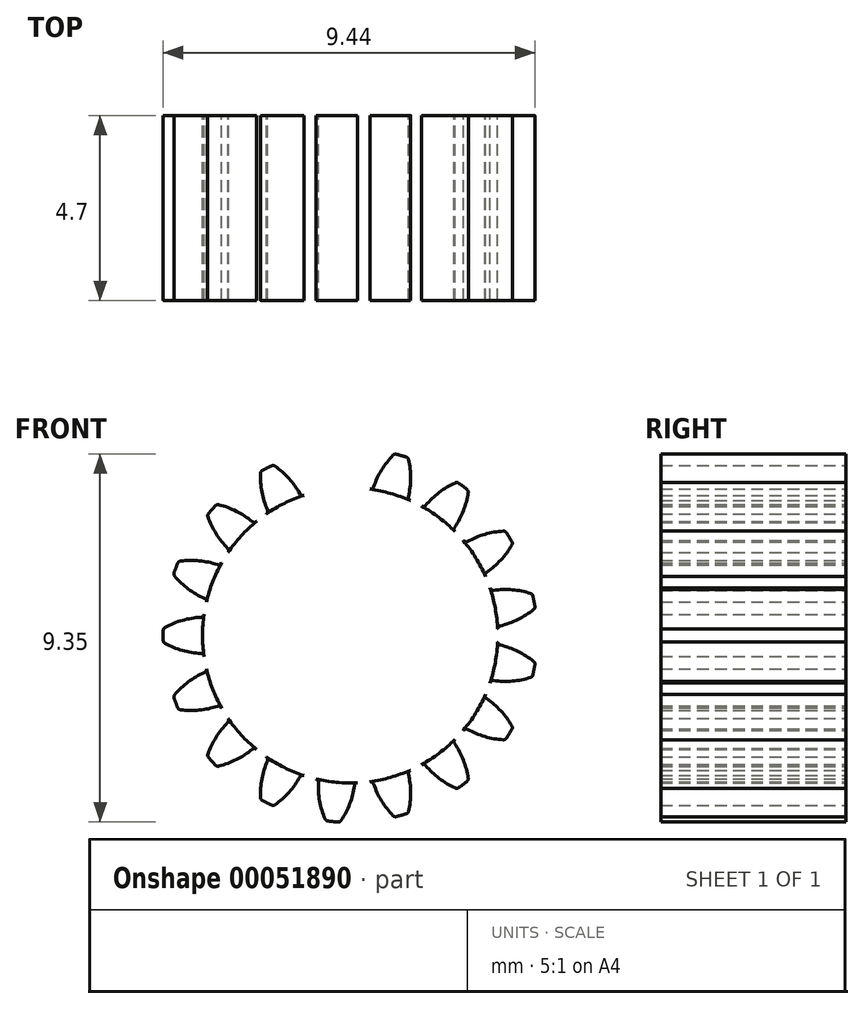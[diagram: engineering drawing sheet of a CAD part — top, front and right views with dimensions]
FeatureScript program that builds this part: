
annotation { "Feature Type Name" : "Feature", "Feature Type Description" : "" }
export const myFeature = defineFeature(function(context is Context, id is Id, definition is map)
    precondition{}
    {
        {
            var Q0;
            Q0=qCreatedBy(makeId("Front.planeOp"),FACE);
            var sketch = newSketch(context, id + "F0", { "sketchPlane" : qUnion([Q0])});
            skCircle(sketch, "E0", {"center": v(0, 0) * mm, "radius": 3.75 * mm, "construction": true});
            skCircle(sketch, "E1", {"center": v(0, 0) * mm, "radius": 4.25 * mm, "construction": true});
            skCircle(sketch, "E2", {"center": v(0, 0) * mm, "radius": 4.75 * mm, "construction": true});
            skLineSegment(sketch, "E3", {"start": v(0, 0) * mm, "end": v(0, 10.28) * mm, "construction": true});
            skLineSegment(sketch, "E4", {"start": v(0, 0) * mm, "end": v(-1.03, 11.12) * mm, "construction": true});
            skLineSegment(sketch, "E5", {"start": v(0, 4.25) * mm, "end": v(-15.76, 4.25) * mm, "construction": true});
            skLineSegment(sketch, "E6", {"start": v(0, 4.25) * mm, "end": v(-14.39, -0.99) * mm, "construction": true});
            skCircle(sketch, "E7", {"center": v(0, 4.25) * mm, "radius": 2.12 * mm, "construction": true});
            skCircle(sketch, "E8", {"center": v(-2, 3.52) * mm, "radius": 2.12 * mm, "construction": true});
            skArc(sketch, "E9", {"start": v(-0.23, 4.7) * mm, "mid": v(-0.01, 4.28) * mm, "end": v(0.1, 3.82) * mm});
            skArc(sketch, "E10.MirrorCS", {"start": v(-0.64, 4.66) * mm, "mid": v(-0.78, 4.2) * mm, "end": v(-0.8, 3.73) * mm});
            skArc(sketch, "E11", {"start": v(-0.57, 4.72) * mm, "mid": v(-0.44, 4.73) * mm, "end": v(-0.3, 4.74) * mm});
            skArc(sketch, "E12", {"start": v(-0.87, 3.65) * mm, "mid": v(0.35, -3.73) * mm, "end": v(0.19, 3.75) * mm});
            skPoint(sketch, "E13.visualSharp", {"position": v(-0.8, 3.66) * mm});
            skArc(sketch, "E13.filletArc", {"start": v(-0.87, 3.65) * mm, "mid": v(-0.82, 3.68) * mm, "end": v(-0.8, 3.73) * mm});
            skPoint(sketch, "E14.visualSharp", {"position": v(-0.62, 4.7) * mm});
            skArc(sketch, "E14.filletArc", {"start": v(-0.57, 4.72) * mm, "mid": v(-0.61, 4.7) * mm, "end": v(-0.64, 4.66) * mm});
            skPoint(sketch, "E15.visualSharp", {"position": v(-0.26, 4.74) * mm});
            skArc(sketch, "E15.filletArc", {"start": v(-0.23, 4.7) * mm, "mid": v(-0.26, 4.73) * mm, "end": v(-0.3, 4.74) * mm});
            skPoint(sketch, "E16.visualSharp", {"position": v(0.12, 3.75) * mm});
            skArc(sketch, "E16.filletArc", {"start": v(0.1, 3.82) * mm, "mid": v(0.13, 3.77) * mm, "end": v(0.19, 3.75) * mm});
            skArc(sketch, "E17.1.0", {"start": v(-2.13, 3.09) * mm, "mid": v(-2.1, 3.13) * mm, "end": v(-2.1, 3.19) * mm});
            skArc(sketch, "E17.1.1", {"start": v(-2.28, 4.12) * mm, "mid": v(-2.24, 3.64) * mm, "end": v(-2.1, 3.19) * mm});
            skArc(sketch, "E17.1.2", {"start": v(-2.24, 4.2) * mm, "mid": v(-2.27, 4.16) * mm, "end": v(-2.28, 4.12) * mm});
            skArc(sketch, "E17.1.3", {"start": v(-2.24, 4.2) * mm, "mid": v(-2.12, 4.25) * mm, "end": v(-2, 4.3) * mm});
            skArc(sketch, "E17.1.4", {"start": v(-1.91, 4.3) * mm, "mid": v(-1.95, 4.32) * mm, "end": v(-2, 4.3) * mm});
            skArc(sketch, "E17.1.5", {"start": v(-1.91, 4.3) * mm, "mid": v(-1.56, 3.99) * mm, "end": v(-1.28, 3.6) * mm});
            skArc(sketch, "E17.1.6", {"start": v(-1.28, 3.6) * mm, "mid": v(-1.24, 3.56) * mm, "end": v(-1.18, 3.56) * mm});
            skArc(sketch, "E17.2.0", {"start": v(-3.1, 2.1) * mm, "mid": v(-3.09, 2.16) * mm, "end": v(-3.11, 2.22) * mm});
            skArc(sketch, "E17.2.1", {"start": v(-3.61, 3.02) * mm, "mid": v(-3.4, 2.59) * mm, "end": v(-3.11, 2.22) * mm});
            skArc(sketch, "E17.2.2", {"start": v(-3.6, 3.1) * mm, "mid": v(-3.62, 3.06) * mm, "end": v(-3.61, 3.02) * mm});
            skArc(sketch, "E17.2.3", {"start": v(-3.6, 3.1) * mm, "mid": v(-3.51, 3.2) * mm, "end": v(-3.42, 3.3) * mm});
            skArc(sketch, "E17.2.4", {"start": v(-3.34, 3.32) * mm, "mid": v(-3.38, 3.32) * mm, "end": v(-3.42, 3.3) * mm});
            skArc(sketch, "E17.2.5", {"start": v(-3.34, 3.32) * mm, "mid": v(-2.9, 3.16) * mm, "end": v(-2.5, 2.9) * mm});
            skArc(sketch, "E17.2.6", {"start": v(-2.5, 2.9) * mm, "mid": v(-2.44, 2.87) * mm, "end": v(-2.38, 2.9) * mm});
            skArc(sketch, "E17.3.0", {"start": v(-3.65, 0.84) * mm, "mid": v(-3.66, 0.9) * mm, "end": v(-3.7, 0.94) * mm});
            skArc(sketch, "E17.3.1", {"start": v(-4.46, 1.5) * mm, "mid": v(-4.11, 1.18) * mm, "end": v(-3.7, 0.94) * mm});
            skArc(sketch, "E17.3.2", {"start": v(-4.48, 1.6) * mm, "mid": v(-4.48, 1.55) * mm, "end": v(-4.46, 1.5) * mm});
            skArc(sketch, "E17.3.3", {"start": v(-4.48, 1.6) * mm, "mid": v(-4.43, 1.72) * mm, "end": v(-4.38, 1.84) * mm});
            skArc(sketch, "E17.3.4", {"start": v(-4.31, 1.9) * mm, "mid": v(-4.35, 1.87) * mm, "end": v(-4.38, 1.84) * mm});
            skArc(sketch, "E17.3.5", {"start": v(-4.31, 1.9) * mm, "mid": v(-3.84, 1.9) * mm, "end": v(-3.37, 1.8) * mm});
            skArc(sketch, "E17.3.6", {"start": v(-3.37, 1.8) * mm, "mid": v(-3.31, 1.8) * mm, "end": v(-3.27, 1.84) * mm});
            skArc(sketch, "E17.4.0", {"start": v(-3.71, -0.53) * mm, "mid": v(-3.74, -0.48) * mm, "end": v(-3.8, -0.46) * mm});
            skArc(sketch, "E17.4.1", {"start": v(-4.7, -0.2) * mm, "mid": v(-4.26, -0.38) * mm, "end": v(-3.8, -0.46) * mm});
            skArc(sketch, "E17.4.2", {"start": v(-4.75, -0.13) * mm, "mid": v(-4.74, -0.18) * mm, "end": v(-4.7, -0.2) * mm});
            skArc(sketch, "E17.4.3", {"start": v(-4.75, -0.13) * mm, "mid": v(-4.75, 0) * mm, "end": v(-4.75, 0.13) * mm});
            skArc(sketch, "E17.4.4", {"start": v(-4.7, 0.2) * mm, "mid": v(-4.74, 0.18) * mm, "end": v(-4.75, 0.13) * mm});
            skArc(sketch, "E17.4.5", {"start": v(-4.7, 0.2) * mm, "mid": v(-4.26, 0.38) * mm, "end": v(-3.8, 0.46) * mm});
            skArc(sketch, "E17.4.6", {"start": v(-3.8, 0.46) * mm, "mid": v(-3.74, 0.48) * mm, "end": v(-3.71, 0.53) * mm});
            skArc(sketch, "E17.5.0", {"start": v(-3.27, -1.84) * mm, "mid": v(-3.31, -1.8) * mm, "end": v(-3.37, -1.8) * mm});
            skArc(sketch, "E17.5.1", {"start": v(-4.31, -1.9) * mm, "mid": v(-3.84, -1.9) * mm, "end": v(-3.37, -1.8) * mm});
            skArc(sketch, "E17.5.2", {"start": v(-4.38, -1.84) * mm, "mid": v(-4.35, -1.87) * mm, "end": v(-4.31, -1.9) * mm});
            skArc(sketch, "E17.5.3", {"start": v(-4.38, -1.84) * mm, "mid": v(-4.43, -1.72) * mm, "end": v(-4.48, -1.6) * mm});
            skArc(sketch, "E17.5.4", {"start": v(-4.46, -1.5) * mm, "mid": v(-4.48, -1.55) * mm, "end": v(-4.48, -1.6) * mm});
            skArc(sketch, "E17.5.5", {"start": v(-4.46, -1.5) * mm, "mid": v(-4.11, -1.18) * mm, "end": v(-3.7, -0.94) * mm});
            skArc(sketch, "E17.5.6", {"start": v(-3.7, -0.94) * mm, "mid": v(-3.66, -0.9) * mm, "end": v(-3.65, -0.84) * mm});
            skArc(sketch, "E17.6.0", {"start": v(-2.38, -2.9) * mm, "mid": v(-2.44, -2.87) * mm, "end": v(-2.5, -2.9) * mm});
            skArc(sketch, "E17.6.1", {"start": v(-3.34, -3.32) * mm, "mid": v(-2.9, -3.16) * mm, "end": v(-2.5, -2.9) * mm});
            skArc(sketch, "E17.6.2", {"start": v(-3.42, -3.3) * mm, "mid": v(-3.38, -3.32) * mm, "end": v(-3.34, -3.32) * mm});
            skArc(sketch, "E17.6.3", {"start": v(-3.42, -3.3) * mm, "mid": v(-3.51, -3.2) * mm, "end": v(-3.6, -3.1) * mm});
            skArc(sketch, "E17.6.4", {"start": v(-3.61, -3.02) * mm, "mid": v(-3.62, -3.06) * mm, "end": v(-3.6, -3.1) * mm});
            skArc(sketch, "E17.6.5", {"start": v(-3.61, -3.02) * mm, "mid": v(-3.4, -2.59) * mm, "end": v(-3.11, -2.22) * mm});
            skArc(sketch, "E17.6.6", {"start": v(-3.11, -2.22) * mm, "mid": v(-3.09, -2.16) * mm, "end": v(-3.1, -2.1) * mm});
            skArc(sketch, "E17.7.0", {"start": v(-1.18, -3.56) * mm, "mid": v(-1.24, -3.56) * mm, "end": v(-1.28, -3.6) * mm});
            skArc(sketch, "E17.7.1", {"start": v(-1.91, -4.3) * mm, "mid": v(-1.56, -3.99) * mm, "end": v(-1.28, -3.6) * mm});
            skArc(sketch, "E17.7.2", {"start": v(-2, -4.3) * mm, "mid": v(-1.95, -4.32) * mm, "end": v(-1.91, -4.3) * mm});
            skArc(sketch, "E17.7.3", {"start": v(-2, -4.3) * mm, "mid": v(-2.12, -4.25) * mm, "end": v(-2.24, -4.2) * mm});
            skArc(sketch, "E17.7.4", {"start": v(-2.28, -4.12) * mm, "mid": v(-2.27, -4.16) * mm, "end": v(-2.24, -4.2) * mm});
            skArc(sketch, "E17.7.5", {"start": v(-2.28, -4.12) * mm, "mid": v(-2.24, -3.64) * mm, "end": v(-2.1, -3.19) * mm});
            skArc(sketch, "E17.7.6", {"start": v(-2.1, -3.19) * mm, "mid": v(-2.1, -3.13) * mm, "end": v(-2.13, -3.09) * mm});
            skArc(sketch, "E17.8.0", {"start": v(0.19, -3.75) * mm, "mid": v(0.13, -3.77) * mm, "end": v(0.1, -3.82) * mm});
            skArc(sketch, "E17.8.1", {"start": v(-0.23, -4.7) * mm, "mid": v(-0.01, -4.28) * mm, "end": v(0.1, -3.82) * mm});
            skArc(sketch, "E17.8.2", {"start": v(-0.3, -4.74) * mm, "mid": v(-0.26, -4.73) * mm, "end": v(-0.23, -4.7) * mm});
            skArc(sketch, "E17.8.3", {"start": v(-0.3, -4.74) * mm, "mid": v(-0.44, -4.73) * mm, "end": v(-0.57, -4.72) * mm});
            skArc(sketch, "E17.8.4", {"start": v(-0.64, -4.66) * mm, "mid": v(-0.61, -4.7) * mm, "end": v(-0.57, -4.72) * mm});
            skArc(sketch, "E17.8.5", {"start": v(-0.64, -4.66) * mm, "mid": v(-0.78, -4.2) * mm, "end": v(-0.8, -3.73) * mm});
            skArc(sketch, "E17.8.6", {"start": v(-0.8, -3.73) * mm, "mid": v(-0.82, -3.68) * mm, "end": v(-0.87, -3.65) * mm});
            skArc(sketch, "E17.9.0", {"start": v(1.53, -3.42) * mm, "mid": v(1.49, -3.46) * mm, "end": v(1.48, -3.52) * mm});
            skArc(sketch, "E17.9.1", {"start": v(1.49, -4.47) * mm, "mid": v(1.54, -4) * mm, "end": v(1.48, -3.52) * mm});
            skArc(sketch, "E17.9.2", {"start": v(1.43, -4.53) * mm, "mid": v(1.46, -4.5) * mm, "end": v(1.49, -4.47) * mm});
            skArc(sketch, "E17.9.3", {"start": v(1.43, -4.53) * mm, "mid": v(1.3, -4.57) * mm, "end": v(1.17, -4.6) * mm});
            skArc(sketch, "E17.9.4", {"start": v(1.09, -4.58) * mm, "mid": v(1.13, -4.6) * mm, "end": v(1.17, -4.6) * mm});
            skArc(sketch, "E17.9.5", {"start": v(1.09, -4.58) * mm, "mid": v(0.8, -4.2) * mm, "end": v(0.6, -3.77) * mm});
            skArc(sketch, "E17.9.6", {"start": v(0.6, -3.77) * mm, "mid": v(0.56, -3.73) * mm, "end": v(0.5, -3.72) * mm});
            skArc(sketch, "E17.10.0", {"start": v(2.66, -2.64) * mm, "mid": v(2.64, -2.7) * mm, "end": v(2.65, -2.75) * mm});
            skArc(sketch, "E17.10.1", {"start": v(3, -3.63) * mm, "mid": v(2.87, -3.17) * mm, "end": v(2.65, -2.75) * mm});
            skArc(sketch, "E17.10.2", {"start": v(2.97, -3.7) * mm, "mid": v(3, -3.67) * mm, "end": v(3, -3.63) * mm});
            skArc(sketch, "E17.10.3", {"start": v(2.97, -3.7) * mm, "mid": v(2.86, -3.8) * mm, "end": v(2.75, -3.87) * mm});
            skArc(sketch, "E17.10.4", {"start": v(2.67, -3.88) * mm, "mid": v(2.71, -3.88) * mm, "end": v(2.75, -3.87) * mm});
            skArc(sketch, "E17.10.5", {"start": v(2.67, -3.88) * mm, "mid": v(2.26, -3.63) * mm, "end": v(1.92, -3.3) * mm});
            skArc(sketch, "E17.10.6", {"start": v(1.92, -3.3) * mm, "mid": v(1.87, -3.27) * mm, "end": v(1.81, -3.28) * mm});
            skArc(sketch, "E17.11.0", {"start": v(3.44, -1.5) * mm, "mid": v(3.43, -1.56) * mm, "end": v(3.47, -1.6) * mm});
            skArc(sketch, "E17.11.1", {"start": v(4.1, -2.3) * mm, "mid": v(3.83, -1.92) * mm, "end": v(3.47, -1.6) * mm});
            skArc(sketch, "E17.11.2", {"start": v(4.1, -2.39) * mm, "mid": v(4.12, -2.34) * mm, "end": v(4.1, -2.3) * mm});
            skArc(sketch, "E17.11.3", {"start": v(4.1, -2.39) * mm, "mid": v(4.04, -2.5) * mm, "end": v(3.97, -2.61) * mm});
            skArc(sketch, "E17.11.4", {"start": v(3.9, -2.65) * mm, "mid": v(3.93, -2.64) * mm, "end": v(3.97, -2.61) * mm});
            skArc(sketch, "E17.11.5", {"start": v(3.9, -2.65) * mm, "mid": v(3.42, -2.57) * mm, "end": v(2.98, -2.39) * mm});
            skArc(sketch, "E17.11.6", {"start": v(2.98, -2.39) * mm, "mid": v(2.93, -2.38) * mm, "end": v(2.88, -2.4) * mm});
            skArc(sketch, "E17.12.0", {"start": v(3.75, -0.16) * mm, "mid": v(3.76, -0.21) * mm, "end": v(3.81, -0.25) * mm});
            skArc(sketch, "E17.12.1", {"start": v(4.66, -0.66) * mm, "mid": v(4.26, -0.4) * mm, "end": v(3.81, -0.25) * mm});
            skArc(sketch, "E17.12.2", {"start": v(4.7, -0.74) * mm, "mid": v(4.69, -0.7) * mm, "end": v(4.66, -0.66) * mm});
            skArc(sketch, "E17.12.3", {"start": v(4.7, -0.74) * mm, "mid": v(4.67, -0.87) * mm, "end": v(4.64, -1) * mm});
            skArc(sketch, "E17.12.4", {"start": v(4.59, -1.07) * mm, "mid": v(4.62, -1.04) * mm, "end": v(4.64, -1) * mm});
            skArc(sketch, "E17.12.5", {"start": v(4.59, -1.07) * mm, "mid": v(4.12, -1.16) * mm, "end": v(3.64, -1.15) * mm});
            skArc(sketch, "E17.12.6", {"start": v(3.64, -1.15) * mm, "mid": v(3.59, -1.16) * mm, "end": v(3.55, -1.2) * mm});
            skArc(sketch, "E17.13.0", {"start": v(3.55, 1.2) * mm, "mid": v(3.59, 1.16) * mm, "end": v(3.64, 1.15) * mm});
            skArc(sketch, "E17.13.1", {"start": v(4.59, 1.07) * mm, "mid": v(4.12, 1.16) * mm, "end": v(3.64, 1.15) * mm});
            skArc(sketch, "E17.13.2", {"start": v(4.64, 1) * mm, "mid": v(4.62, 1.04) * mm, "end": v(4.59, 1.07) * mm});
            skArc(sketch, "E17.13.3", {"start": v(4.64, 1) * mm, "mid": v(4.67, 0.87) * mm, "end": v(4.7, 0.74) * mm});
            skArc(sketch, "E17.13.4", {"start": v(4.66, 0.66) * mm, "mid": v(4.69, 0.7) * mm, "end": v(4.7, 0.74) * mm});
            skArc(sketch, "E17.13.5", {"start": v(4.66, 0.66) * mm, "mid": v(4.26, 0.4) * mm, "end": v(3.81, 0.25) * mm});
            skArc(sketch, "E17.13.6", {"start": v(3.81, 0.25) * mm, "mid": v(3.76, 0.21) * mm, "end": v(3.75, 0.16) * mm});
            skArc(sketch, "E17.14.0", {"start": v(2.88, 2.4) * mm, "mid": v(2.93, 2.38) * mm, "end": v(2.98, 2.39) * mm});
            skArc(sketch, "E17.14.1", {"start": v(3.9, 2.65) * mm, "mid": v(3.42, 2.57) * mm, "end": v(2.98, 2.39) * mm});
            skArc(sketch, "E17.14.2", {"start": v(3.97, 2.61) * mm, "mid": v(3.93, 2.64) * mm, "end": v(3.9, 2.65) * mm});
            skArc(sketch, "E17.14.3", {"start": v(3.97, 2.61) * mm, "mid": v(4.04, 2.5) * mm, "end": v(4.1, 2.39) * mm});
            skArc(sketch, "E17.14.4", {"start": v(4.1, 2.3) * mm, "mid": v(4.12, 2.34) * mm, "end": v(4.1, 2.39) * mm});
            skArc(sketch, "E17.14.5", {"start": v(4.1, 2.3) * mm, "mid": v(3.83, 1.92) * mm, "end": v(3.47, 1.6) * mm});
            skArc(sketch, "E17.14.6", {"start": v(3.47, 1.6) * mm, "mid": v(3.43, 1.56) * mm, "end": v(3.44, 1.5) * mm});
            skArc(sketch, "E17.15.0", {"start": v(1.81, 3.28) * mm, "mid": v(1.87, 3.27) * mm, "end": v(1.92, 3.3) * mm});
            skArc(sketch, "E17.15.1", {"start": v(2.67, 3.88) * mm, "mid": v(2.26, 3.63) * mm, "end": v(1.92, 3.3) * mm});
            skArc(sketch, "E17.15.2", {"start": v(2.75, 3.87) * mm, "mid": v(2.71, 3.88) * mm, "end": v(2.67, 3.88) * mm});
            skArc(sketch, "E17.15.3", {"start": v(2.75, 3.87) * mm, "mid": v(2.86, 3.8) * mm, "end": v(2.97, 3.7) * mm});
            skArc(sketch, "E17.15.4", {"start": v(3, 3.63) * mm, "mid": v(3, 3.67) * mm, "end": v(2.97, 3.7) * mm});
            skArc(sketch, "E17.15.5", {"start": v(3, 3.63) * mm, "mid": v(2.87, 3.17) * mm, "end": v(2.65, 2.75) * mm});
            skArc(sketch, "E17.15.6", {"start": v(2.65, 2.75) * mm, "mid": v(2.64, 2.7) * mm, "end": v(2.66, 2.64) * mm});
            skArc(sketch, "E17.16.0", {"start": v(0.5, 3.72) * mm, "mid": v(0.56, 3.73) * mm, "end": v(0.6, 3.77) * mm});
            skArc(sketch, "E17.16.1", {"start": v(1.09, 4.58) * mm, "mid": v(0.8, 4.2) * mm, "end": v(0.6, 3.77) * mm});
            skArc(sketch, "E17.16.2", {"start": v(1.17, 4.6) * mm, "mid": v(1.13, 4.6) * mm, "end": v(1.09, 4.58) * mm});
            skArc(sketch, "E17.16.3", {"start": v(1.17, 4.6) * mm, "mid": v(1.3, 4.57) * mm, "end": v(1.43, 4.53) * mm});
            skArc(sketch, "E17.16.4", {"start": v(1.49, 4.47) * mm, "mid": v(1.46, 4.5) * mm, "end": v(1.43, 4.53) * mm});
            skArc(sketch, "E17.16.5", {"start": v(1.49, 4.47) * mm, "mid": v(1.54, 4) * mm, "end": v(1.48, 3.52) * mm});
            skArc(sketch, "E17.16.6", {"start": v(1.48, 3.52) * mm, "mid": v(1.49, 3.46) * mm, "end": v(1.53, 3.42) * mm});
            skSolve(sketch);
        }
        {
            var Q0;
            Q0=makeQuery(id+"F0.imprint","IMPRINT",FACE,{"disambiguationData":[TD([[makeQuery(id+"F0.imprint","IMPRINT",EDGE,{"derivedFrom":sQuery(id+"F0.wireOp",EDGE,"E9")}),-1.0]])]});
            var Q1;
            {var subQ0=sQuery(id+"F0.wireOp",EDGE,"E17.1.0");Q1=makeQuery(id+"F0.imprint","IMPRINT",FACE,{"disambiguationData":[TD([[makeQuery(id+"F0.imprint","IMPRINT",EDGE,{"derivedFrom":subQ0}),-1.0]])]});}
            var Q2;
            {var subQ0=sQuery(id+"F0.wireOp",EDGE,"E17.2.0");Q2=makeQuery(id+"F0.imprint","IMPRINT",FACE,{"disambiguationData":[TD([[makeQuery(id+"F0.imprint","IMPRINT",EDGE,{"derivedFrom":subQ0}),-1.0]])]});}
            var Q3;
            {var subQ0=sQuery(id+"F0.wireOp",EDGE,"E17.3.0");Q3=makeQuery(id+"F0.imprint","IMPRINT",FACE,{"disambiguationData":[TD([[makeQuery(id+"F0.imprint","IMPRINT",EDGE,{"derivedFrom":subQ0}),-1.0]])]});}
            var Q4;
            {var subQ0=sQuery(id+"F0.wireOp",EDGE,"E17.4.0");Q4=makeQuery(id+"F0.imprint","IMPRINT",FACE,{"disambiguationData":[TD([[makeQuery(id+"F0.imprint","IMPRINT",EDGE,{"derivedFrom":subQ0}),-1.0]])]});}
            var Q5;
            {var subQ0=sQuery(id+"F0.wireOp",EDGE,"E17.16.0");Q5=makeQuery(id+"F0.imprint","IMPRINT",FACE,{"disambiguationData":[TD([[makeQuery(id+"F0.imprint","IMPRINT",EDGE,{"derivedFrom":subQ0}),-1.0]])]});}
            var Q6;
            {var subQ0=sQuery(id+"F0.wireOp",EDGE,"E17.15.0");Q6=makeQuery(id+"F0.imprint","IMPRINT",FACE,{"disambiguationData":[TD([[makeQuery(id+"F0.imprint","IMPRINT",EDGE,{"derivedFrom":subQ0}),-1.0]])]});}
            var Q7;
            {var subQ1=sQuery(id+"F0.wireOp",EDGE,"E17.14.0");Q7=makeQuery(id+"F0.imprint","IMPRINT",FACE,{"disambiguationData":[TD([[makeQuery(id+"F0.imprint","IMPRINT",EDGE,{"derivedFrom":subQ1}),-1.0]])]});}
            var Q8;
            {var subQ0=sQuery(id+"F0.wireOp",EDGE,"E17.13.0");Q8=makeQuery(id+"F0.imprint","IMPRINT",FACE,{"disambiguationData":[TD([[makeQuery(id+"F0.imprint","IMPRINT",EDGE,{"derivedFrom":subQ0}),-1.0]])]});}
            var Q9;
            {var subQ1=sQuery(id+"F0.wireOp",EDGE,"E17.12.0");Q9=makeQuery(id+"F0.imprint","IMPRINT",FACE,{"disambiguationData":[TD([[makeQuery(id+"F0.imprint","IMPRINT",EDGE,{"derivedFrom":subQ1}),-1.0]])]});}
            var Q10;
            {var subQ0=sQuery(id+"F0.wireOp",EDGE,"E17.11.0");Q10=makeQuery(id+"F0.imprint","IMPRINT",FACE,{"disambiguationData":[TD([[makeQuery(id+"F0.imprint","IMPRINT",EDGE,{"derivedFrom":subQ0}),-1.0]])]});}
            var Q11;
            {var subQ0=sQuery(id+"F0.wireOp",EDGE,"E17.10.0");Q11=makeQuery(id+"F0.imprint","IMPRINT",FACE,{"disambiguationData":[TD([[makeQuery(id+"F0.imprint","IMPRINT",EDGE,{"derivedFrom":subQ0}),-1.0]])]});}
            var Q12;
            {var subQ0=sQuery(id+"F0.wireOp",EDGE,"E17.9.0");Q12=makeQuery(id+"F0.imprint","IMPRINT",FACE,{"disambiguationData":[TD([[makeQuery(id+"F0.imprint","IMPRINT",EDGE,{"derivedFrom":subQ0}),-1.0]])]});}
            var Q13;
            {var subQ0=sQuery(id+"F0.wireOp",EDGE,"E17.8.0");Q13=makeQuery(id+"F0.imprint","IMPRINT",FACE,{"disambiguationData":[TD([[makeQuery(id+"F0.imprint","IMPRINT",EDGE,{"derivedFrom":subQ0}),-1.0]])]});}
            var Q14;
            {var subQ0=sQuery(id+"F0.wireOp",EDGE,"E17.7.0");Q14=makeQuery(id+"F0.imprint","IMPRINT",FACE,{"disambiguationData":[TD([[makeQuery(id+"F0.imprint","IMPRINT",EDGE,{"derivedFrom":subQ0}),-1.0]])]});}
            var Q15;
            {var subQ0=sQuery(id+"F0.wireOp",EDGE,"E17.6.0");Q15=makeQuery(id+"F0.imprint","IMPRINT",FACE,{"disambiguationData":[TD([[makeQuery(id+"F0.imprint","IMPRINT",EDGE,{"derivedFrom":subQ0}),-1.0]])]});}
            var Q16;
            {var subQ0=sQuery(id+"F0.wireOp",EDGE,"E17.5.0");Q16=makeQuery(id+"F0.imprint","IMPRINT",FACE,{"disambiguationData":[TD([[makeQuery(id+"F0.imprint","IMPRINT",EDGE,{"derivedFrom":subQ0}),-1.0]])]});}
            extrude(context, id + "F1", {"entities" : qUnion([Q0, Q1, Q2, Q3, Q4, Q5, Q6, Q7, Q8, Q9, Q10, Q11, Q12, Q13, Q14, Q15, Q16]), "depth" : 4.7 * mm});
        }
        {
            var Q0;
            Q0=makeQuery(id+"F1.opExtrude","CAP_FACE",FACE,{"disambiguationData":[OSD([sQuery(id+"F0.wireOp",EDGE,"E9"),sQuery(id+"F0.wireOp",EDGE,"E10.MirrorCS"),sQuery(id+"F0.wireOp",EDGE,"E11"),sQuery(id+"F0.wireOp",EDGE,"E12"),sQuery(id+"F0.wireOp",EDGE,"E13.filletArc"),sQuery(id+"F0.wireOp",EDGE,"E14.filletArc"),sQuery(id+"F0.wireOp",EDGE,"E15.filletArc"),sQuery(id+"F0.wireOp",EDGE,"E16.filletArc"),sQuery(id+"F0.wireOp",EDGE,"E17.1.0"),sQuery(id+"F0.wireOp",EDGE,"E17.1.1"),sQuery(id+"F0.wireOp",EDGE,"E17.1.2"),sQuery(id+"F0.wireOp",EDGE,"E17.1.3"),sQuery(id+"F0.wireOp",EDGE,"E17.1.4"),sQuery(id+"F0.wireOp",EDGE,"E17.1.5"),sQuery(id+"F0.wireOp",EDGE,"E17.1.6"),sQuery(id+"F0.wireOp",EDGE,"E17.2.0"),sQuery(id+"F0.wireOp",EDGE,"E17.2.1"),sQuery(id+"F0.wireOp",EDGE,"E17.2.2"),sQuery(id+"F0.wireOp",EDGE,"E17.2.3"),sQuery(id+"F0.wireOp",EDGE,"E17.2.4"),sQuery(id+"F0.wireOp",EDGE,"E17.2.5"),sQuery(id+"F0.wireOp",EDGE,"E17.2.6"),sQuery(id+"F0.wireOp",EDGE,"E17.3.0"),sQuery(id+"F0.wireOp",EDGE,"E17.3.1"),sQuery(id+"F0.wireOp",EDGE,"E17.3.2"),sQuery(id+"F0.wireOp",EDGE,"E17.3.3"),sQuery(id+"F0.wireOp",EDGE,"E17.3.4"),sQuery(id+"F0.wireOp",EDGE,"E17.3.5"),sQuery(id+"F0.wireOp",EDGE,"E17.3.6"),sQuery(id+"F0.wireOp",EDGE,"E17.4.0"),sQuery(id+"F0.wireOp",EDGE,"E17.4.1"),sQuery(id+"F0.wireOp",EDGE,"E17.4.2"),sQuery(id+"F0.wireOp",EDGE,"E17.4.3"),sQuery(id+"F0.wireOp",EDGE,"E17.4.4"),sQuery(id+"F0.wireOp",EDGE,"E17.4.5"),sQuery(id+"F0.wireOp",EDGE,"E17.4.6"),sQuery(id+"F0.wireOp",EDGE,"E17.5.0"),sQuery(id+"F0.wireOp",EDGE,"E17.5.1"),sQuery(id+"F0.wireOp",EDGE,"E17.5.2"),sQuery(id+"F0.wireOp",EDGE,"E17.5.3"),sQuery(id+"F0.wireOp",EDGE,"E17.5.4"),sQuery(id+"F0.wireOp",EDGE,"E17.5.5"),sQuery(id+"F0.wireOp",EDGE,"E17.5.6"),sQuery(id+"F0.wireOp",EDGE,"E17.6.0"),sQuery(id+"F0.wireOp",EDGE,"E17.6.1"),sQuery(id+"F0.wireOp",EDGE,"E17.6.2"),sQuery(id+"F0.wireOp",EDGE,"E17.6.3"),sQuery(id+"F0.wireOp",EDGE,"E17.6.4"),sQuery(id+"F0.wireOp",EDGE,"E17.6.5"),sQuery(id+"F0.wireOp",EDGE,"E17.6.6"),sQuery(id+"F0.wireOp",EDGE,"E17.7.0"),sQuery(id+"F0.wireOp",EDGE,"E17.7.1"),sQuery(id+"F0.wireOp",EDGE,"E17.7.2"),sQuery(id+"F0.wireOp",EDGE,"E17.7.3"),sQuery(id+"F0.wireOp",EDGE,"E17.7.4"),sQuery(id+"F0.wireOp",EDGE,"E17.7.5"),sQuery(id+"F0.wireOp",EDGE,"E17.7.6"),sQuery(id+"F0.wireOp",EDGE,"E17.8.0"),sQuery(id+"F0.wireOp",EDGE,"E17.8.1"),sQuery(id+"F0.wireOp",EDGE,"E17.8.2"),sQuery(id+"F0.wireOp",EDGE,"E17.8.3"),sQuery(id+"F0.wireOp",EDGE,"E17.8.4"),sQuery(id+"F0.wireOp",EDGE,"E17.8.5"),sQuery(id+"F0.wireOp",EDGE,"E17.8.6"),sQuery(id+"F0.wireOp",EDGE,"E17.9.0"),sQuery(id+"F0.wireOp",EDGE,"E17.9.1"),sQuery(id+"F0.wireOp",EDGE,"E17.9.2"),sQuery(id+"F0.wireOp",EDGE,"E17.9.3"),sQuery(id+"F0.wireOp",EDGE,"E17.9.4"),sQuery(id+"F0.wireOp",EDGE,"E17.9.5"),sQuery(id+"F0.wireOp",EDGE,"E17.9.6"),sQuery(id+"F0.wireOp",EDGE,"E17.10.0"),sQuery(id+"F0.wireOp",EDGE,"E17.10.1"),sQuery(id+"F0.wireOp",EDGE,"E17.10.2"),sQuery(id+"F0.wireOp",EDGE,"E17.10.3"),sQuery(id+"F0.wireOp",EDGE,"E17.10.4"),sQuery(id+"F0.wireOp",EDGE,"E17.10.5"),sQuery(id+"F0.wireOp",EDGE,"E17.10.6"),sQuery(id+"F0.wireOp",EDGE,"E17.11.0"),sQuery(id+"F0.wireOp",EDGE,"E17.11.1"),sQuery(id+"F0.wireOp",EDGE,"E17.11.2"),sQuery(id+"F0.wireOp",EDGE,"E17.11.3"),sQuery(id+"F0.wireOp",EDGE,"E17.11.4"),sQuery(id+"F0.wireOp",EDGE,"E17.11.5"),sQuery(id+"F0.wireOp",EDGE,"E17.11.6"),sQuery(id+"F0.wireOp",EDGE,"E17.12.0"),sQuery(id+"F0.wireOp",EDGE,"E17.12.1"),sQuery(id+"F0.wireOp",EDGE,"E17.12.2"),sQuery(id+"F0.wireOp",EDGE,"E17.12.3"),sQuery(id+"F0.wireOp",EDGE,"E17.12.4"),sQuery(id+"F0.wireOp",EDGE,"E17.12.5"),sQuery(id+"F0.wireOp",EDGE,"E17.12.6"),sQuery(id+"F0.wireOp",EDGE,"E17.13.0"),sQuery(id+"F0.wireOp",EDGE,"E17.13.1"),sQuery(id+"F0.wireOp",EDGE,"E17.13.2"),sQuery(id+"F0.wireOp",EDGE,"E17.13.3"),sQuery(id+"F0.wireOp",EDGE,"E17.13.4"),sQuery(id+"F0.wireOp",EDGE,"E17.13.5"),sQuery(id+"F0.wireOp",EDGE,"E17.13.6"),sQuery(id+"F0.wireOp",EDGE,"E17.14.0"),sQuery(id+"F0.wireOp",EDGE,"E17.14.1"),sQuery(id+"F0.wireOp",EDGE,"E17.14.2"),sQuery(id+"F0.wireOp",EDGE,"E17.14.3"),sQuery(id+"F0.wireOp",EDGE,"E17.14.4"),sQuery(id+"F0.wireOp",EDGE,"E17.14.5"),sQuery(id+"F0.wireOp",EDGE,"E17.14.6"),sQuery(id+"F0.wireOp",EDGE,"E17.15.0"),sQuery(id+"F0.wireOp",EDGE,"E17.15.1"),sQuery(id+"F0.wireOp",EDGE,"E17.15.2"),sQuery(id+"F0.wireOp",EDGE,"E17.15.3"),sQuery(id+"F0.wireOp",EDGE,"E17.15.4"),sQuery(id+"F0.wireOp",EDGE,"E17.15.5"),sQuery(id+"F0.wireOp",EDGE,"E17.15.6"),sQuery(id+"F0.wireOp",EDGE,"E17.16.0"),sQuery(id+"F0.wireOp",EDGE,"E17.16.1"),sQuery(id+"F0.wireOp",EDGE,"E17.16.2"),sQuery(id+"F0.wireOp",EDGE,"E17.16.3"),sQuery(id+"F0.wireOp",EDGE,"E17.16.4"),sQuery(id+"F0.wireOp",EDGE,"E17.16.5"),sQuery(id+"F0.wireOp",EDGE,"E17.16.6")])],"isStart":false});
            var sketch = newSketch(context, id + "F2", { "sketchPlane" : qUnion([Q0])});
            skCircle(sketch, "E18", {"center": v(0, 0) * mm, "radius": 1 * mm});
            skSolve(sketch);
        }
        {
            var Q0;
            Q0 = qSketchRegion(id + "F2", true);
            extrude(context, id + "F3", {"entities" : qUnion([Q0]), "operationType" : NewBodyOperationType.REMOVE, "endBound" : BoundingType.THROUGH_ALL, "oppositeDirection" : true, "depth" : 25 * mm});
        }
    });
